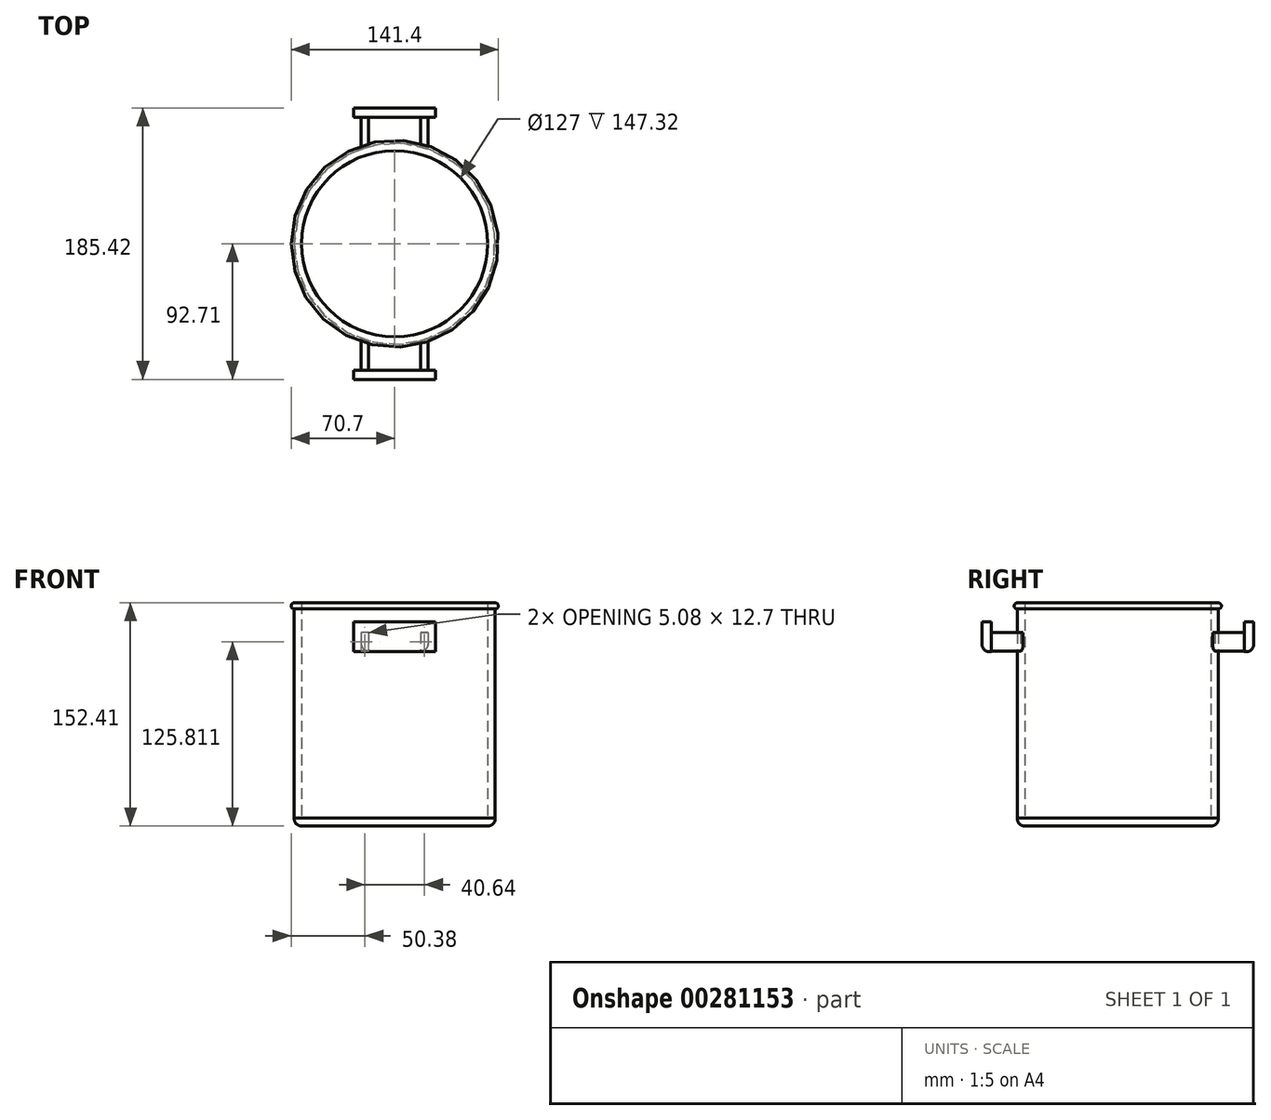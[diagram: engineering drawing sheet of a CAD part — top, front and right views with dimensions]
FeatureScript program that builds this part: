
annotation { "Feature Type Name" : "Feature", "Feature Type Description" : "" }
export const myFeature = defineFeature(function(context is Context, id is Id, definition is map)
    precondition{}
    {
        {
            var Q0;
            Q0=qCreatedBy(makeId("Right.planeOp"),FACE);
            var sketch = newSketch(context, id + "F0", { "sketchPlane" : qUnion([Q0])});
            skLineSegment(sketch, "E0", {"start": v(0, 5.08) * mm, "end": v(63.5, 5.08) * mm});
            skLineSegment(sketch, "E1", {"start": v(63.5, 5.08) * mm, "end": v(63.5, 152.4) * mm});
            skLineSegment(sketch, "E2", {"start": v(63.5, 152.4) * mm, "end": v(68.58, 152.4) * mm});
            skLineSegment(sketch, "E3", {"start": v(0, 0) * mm, "end": v(0, 5.08) * mm});
            skArc(sketch, "E4", {"start": v(68.58, 148.15) * mm, "mid": v(70.7, 150.28) * mm, "end": v(68.58, 152.4) * mm});
            skArc(sketch, "E5", {"start": v(63.32, 0) * mm, "mid": v(67.24, 1.57) * mm, "end": v(68.58, 5.57) * mm});
            skLineSegment(sketch, "E6", {"start": v(0, 0) * mm, "end": v(63.32, 0) * mm});
            skLineSegment(sketch, "E7", {"start": v(68.58, 148.15) * mm, "end": v(68.58, 5.57) * mm});
            skSolve(sketch);
        }
        {
            var Q0;
            Q0 = qSketchRegion(id + "F0", true);
            var Q1;
            Q1=sQuery(id+"F0.wireOp",EDGE,"E3");
            revolve(context, id + "F1", {"entities" : qUnion([Q0]), "axis" : qUnion([Q1]), "revolveType" : RevolveType.FULL});
        }
        {
            var Q0;
            Q0=qCreatedBy(makeId("Front.planeOp"),FACE);
            cPlane(context, id + "F2", {"entities" : qUnion([Q0]), "cplaneType" : CPlaneType.OFFSET, "offset" : 86.36 * mm, "width" : 152.4 * mm, "height" : 152.4 * mm});
        }
        {
            var Q0;
            Q0=qCreatedBy(id+"F2.planeOp",FACE);
            var sketch = newSketch(context, id + "F3", { "sketchPlane" : qUnion([Q0])});
            skLineSegment(sketch, "E8.bottom", {"start": v(-17.78, 119.45) * mm, "end": v(-22.86, 119.45) * mm});
            skLineSegment(sketch, "E8.top", {"start": v(-17.78, 132.15) * mm, "end": v(-22.86, 132.15) * mm});
            skLineSegment(sketch, "E8.left", {"start": v(-17.78, 119.45) * mm, "end": v(-17.78, 132.15) * mm});
            skLineSegment(sketch, "E8.right", {"start": v(-22.86, 119.45) * mm, "end": v(-22.86, 132.15) * mm});
            skPoint(sketch, "E8.middle", {"position": v(-20.32, 125.8) * mm});
            skLineSegment(sketch, "E9.MirrorCS", {"start": v(17.78, 119.45) * mm, "end": v(17.78, 132.15) * mm});
            skLineSegment(sketch, "E10.MirrorCS", {"start": v(17.78, 132.15) * mm, "end": v(22.86, 132.15) * mm});
            skLineSegment(sketch, "E11.MirrorCS", {"start": v(22.86, 119.45) * mm, "end": v(22.86, 132.15) * mm});
            skLineSegment(sketch, "E12.MirrorCS", {"start": v(17.78, 119.45) * mm, "end": v(22.86, 119.45) * mm});
            skSolve(sketch);
        }
        {
            var Q0;
            Q0 = qSketchRegion(id + "F3", true);
            extrude(context, id + "F4", {"entities" : qUnion([Q0]), "operationType" : NewBodyOperationType.ADD, "endBound" : BoundingType.UP_TO_NEXT, "oppositeDirection" : true, "depth" : 25.4 * mm});
        }
        {
            var Q0;
            Q0=qCreatedBy(id+"F2.planeOp",FACE);
            cPlane(context, id + "F5", {"entities" : qUnion([Q0]), "cplaneType" : CPlaneType.OFFSET, "offset" : 6.35 * mm, "width" : 152.4 * mm, "height" : 152.4 * mm});
        }
        {
            var Q0;
            Q0=qCreatedBy(id+"F5.planeOp",FACE);
            var sketch = newSketch(context, id + "F6", { "sketchPlane" : qUnion([Q0])});
            skLineSegment(sketch, "E13.bottom", {"start": v(-27.94, 139.26) * mm, "end": v(27.94, 139.26) * mm});
            skLineSegment(sketch, "E13.top", {"start": v(-27.94, 118.94) * mm, "end": v(27.94, 118.94) * mm});
            skLineSegment(sketch, "E13.left", {"start": v(-27.94, 139.26) * mm, "end": v(-27.94, 118.94) * mm});
            skLineSegment(sketch, "E13.right", {"start": v(27.94, 139.26) * mm, "end": v(27.94, 118.94) * mm});
            skSolve(sketch);
        }
        {
            var Q0;
            Q0 = qSketchRegion(id + "F6", true);
            var Q1;
            Q1=makeQuery(id+"F4.opExtrude","CAP_FACE",FACE,{"disambiguationData":[OSD([sQuery(id+"F3.wireOp",EDGE,"E8.bottom"),sQuery(id+"F3.wireOp",EDGE,"E8.top"),sQuery(id+"F3.wireOp",EDGE,"E8.left"),sQuery(id+"F3.wireOp",EDGE,"E8.right")])],"isStart":true});
            extrude(context, id + "F7", {"entities" : qUnion([Q0]), "operationType" : NewBodyOperationType.ADD, "endBound" : BoundingType.UP_TO_SURFACE, "oppositeDirection" : true, "endBoundEntityFace" : qUnion([Q1]), "depth" : 25.4 * mm});
        }
        {
            var Q0;
            Q0=qCreatedBy(makeId("Front.planeOp"),FACE);
            cPlane(context, id + "F8", {"entities" : qUnion([Q0]), "cplaneType" : CPlaneType.OFFSET, "offset" : 86.36 * mm, "oppositeDirection" : true, "width" : 152.4 * mm, "height" : 152.4 * mm});
        }
        {
            var Q0;
            Q0=qCreatedBy(id+"F8.planeOp",FACE);
            cPlane(context, id + "F9", {"entities" : qUnion([Q0]), "cplaneType" : CPlaneType.OFFSET, "offset" : 6.35 * mm, "oppositeDirection" : true, "width" : 152.4 * mm, "height" : 152.4 * mm});
        }
        {
            var Q0;
            Q0=qCreatedBy(id+"F8.planeOp",FACE);
            var sketch = newSketch(context, id + "F10", { "sketchPlane" : qUnion([Q0])});
            skLineSegment(sketch, "E14.bottom", {"start": v(22.86, 132.15) * mm, "end": v(17.78, 132.15) * mm});
            skLineSegment(sketch, "E14.top", {"start": v(22.86, 119.45) * mm, "end": v(17.78, 119.45) * mm});
            skLineSegment(sketch, "E14.left", {"start": v(22.86, 132.15) * mm, "end": v(22.86, 119.45) * mm});
            skLineSegment(sketch, "E14.right", {"start": v(17.78, 132.15) * mm, "end": v(17.78, 119.45) * mm});
            skLineSegment(sketch, "E15.MirrorCS", {"start": v(-17.78, 132.15) * mm, "end": v(-17.78, 119.45) * mm});
            skLineSegment(sketch, "E16.MirrorCS", {"start": v(-22.86, 132.15) * mm, "end": v(-17.78, 132.15) * mm});
            skLineSegment(sketch, "E17.MirrorCS", {"start": v(-22.86, 132.15) * mm, "end": v(-22.86, 119.45) * mm});
            skLineSegment(sketch, "E18.MirrorCS", {"start": v(-22.86, 119.45) * mm, "end": v(-17.78, 119.45) * mm});
            skSolve(sketch);
        }
        {
            var Q0;
            Q0 = qSketchRegion(id + "F10", true);
            var Q1;
            Q1=makeQuery(id+"F1.opRevolve","SWEPT_FACE",FACE,{"disambiguationData":[OSD([sQuery(id+"F0.wireOp",EDGE,"E7")])]});
            extrude(context, id + "F11", {"entities" : qUnion([Q0]), "operationType" : NewBodyOperationType.ADD, "endBound" : BoundingType.UP_TO_SURFACE, "endBoundEntityFace" : qUnion([Q1]), "depth" : 25.4 * mm});
        }
        {
            var Q0;
            Q0=qCreatedBy(id+"F9.planeOp",FACE);
            var sketch = newSketch(context, id + "F12", { "sketchPlane" : qUnion([Q0])});
            skLineSegment(sketch, "E19.bottom", {"start": v(27.94, 139.26) * mm, "end": v(-27.94, 139.26) * mm});
            skLineSegment(sketch, "E19.top", {"start": v(27.94, 118.94) * mm, "end": v(-27.94, 118.94) * mm});
            skLineSegment(sketch, "E19.left", {"start": v(27.94, 139.26) * mm, "end": v(27.94, 118.94) * mm});
            skLineSegment(sketch, "E19.right", {"start": v(-27.94, 139.26) * mm, "end": v(-27.94, 118.94) * mm});
            skSolve(sketch);
        }
        {
            var Q0;
            Q0 = qSketchRegion(id + "F12", true);
            var Q1;
            Q1=makeQuery(id+"F11.opExtrude","CAP_FACE",FACE,{"disambiguationData":[OSD([sQuery(id+"F10.wireOp",EDGE,"E14.bottom"),sQuery(id+"F10.wireOp",EDGE,"E14.top"),sQuery(id+"F10.wireOp",EDGE,"E14.left"),sQuery(id+"F10.wireOp",EDGE,"E14.right")])],"isStart":true});
            extrude(context, id + "F13", {"entities" : qUnion([Q0]), "operationType" : NewBodyOperationType.ADD, "endBound" : BoundingType.UP_TO_SURFACE, "endBoundEntityFace" : qUnion([Q1]), "depth" : 25.4 * mm});
        }
        {
            var Q0;
            Q0=makeQuery(id+"F7.opExtrude","CAP_EDGE",EDGE,{"disambiguationData":[OSD([sQuery(id+"F6.wireOp",EDGE,"E13.top")])],"isStart":true});
            fillet(context, id + "F14", {"entities" : qUnion([Q0]), "radius" : 5.08 * mm, "tangentPropagation" : true, "allowEdgeOverflow" : false});
        }
        {
            var Q0;
            Q0=makeQuery(id+"F13.opExtrude","CAP_EDGE",EDGE,{"disambiguationData":[OSD([sQuery(id+"F12.wireOp",EDGE,"E19.top")])],"isStart":true});
            fillet(context, id + "F15", {"entities" : qUnion([Q0]), "radius" : 5.08 * mm, "tangentPropagation" : true, "allowEdgeOverflow" : false});
        }
        {
            var Q0;
            Q0=makeQuery(id+"F11.opExtrude","SWEPT_EDGE",EDGE,{"disambiguationData":[OSD([sQuery(id+"F10.wireOp",EDGE,"E17.MirrorCS"),sQuery(id+"F10.wireOp",EDGE,"E18.MirrorCS")])]});
            var Q1;
            Q1=makeQuery(id+"F11.opExtrude","SWEPT_EDGE",EDGE,{"disambiguationData":[OSD([sQuery(id+"F10.wireOp",EDGE,"E14.top"),sQuery(id+"F10.wireOp",EDGE,"E14.left")])]});
            var Q2;
            Q2=makeQuery(id+"F4.opExtrude","SWEPT_EDGE",EDGE,{"disambiguationData":[OSD([sQuery(id+"F3.wireOp",EDGE,"E8.bottom"),sQuery(id+"F3.wireOp",EDGE,"E8.right")])]});
            var Q3;
            Q3=makeQuery(id+"F4.opExtrude","SWEPT_EDGE",EDGE,{"disambiguationData":[OSD([sQuery(id+"F3.wireOp",EDGE,"E11.MirrorCS"),sQuery(id+"F3.wireOp",EDGE,"E12.MirrorCS")])]});
            fillet(context, id + "F16", {"entities" : qUnion([Q0, Q1, Q2, Q3]), "radius" : 5.08 * mm, "tangentPropagation" : true, "allowEdgeOverflow" : false});
        }
    });
